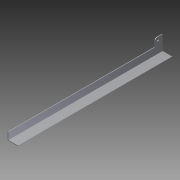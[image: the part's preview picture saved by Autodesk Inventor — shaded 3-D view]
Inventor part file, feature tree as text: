
AUTODESK INVENTOR PART (.ipt)
format: ipt  version: 2012 (Build 160160000, 160)  size: 91,648 bytes
history: native  units: in
note: dims shown in document units (in); Inventor stores cm internally (conversion verified against a paired STEP export)
features: extrude x2, sketch x2
ambient origin geometry x8: Origin, YZ Plane, XZ Plane, XY Plane, X Axis, Y Axis, Z Axis, Center Point
bodies: Solid1 (feature_tree)
feature tree (4):
  extrude  "Extrusion1"  Depth=0.0625in
  extrude  "Extrusion2"  Depth=1.5in
  sketch  "Sketch1"  dims[d0=0.0625in d1=0.0625in]
  sketch  "Sketch2"  dims[d2=1.0in d3=1.5in d4=15.125in d5=0.0in d6=0.75in d7=0.75in d8=0.25in d9=0.5in d10=0.25in d11=1.0in d12=0.0in]
